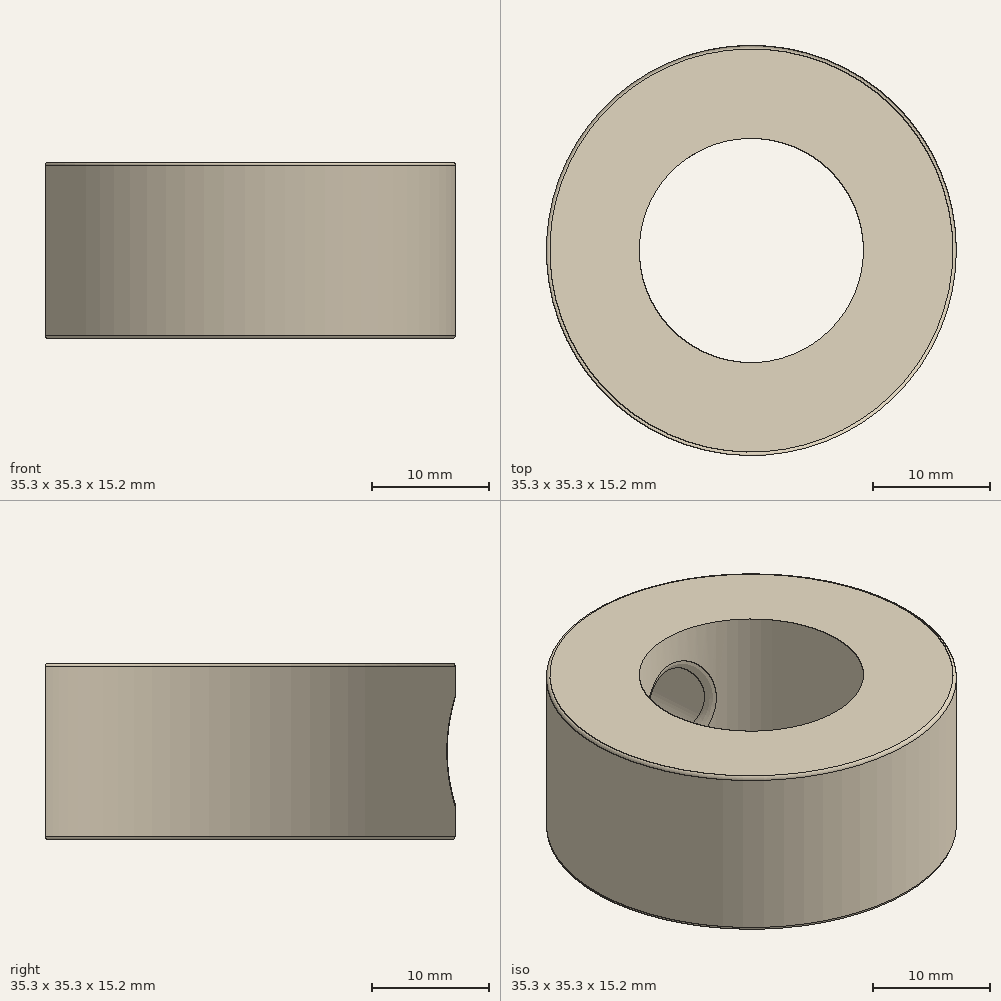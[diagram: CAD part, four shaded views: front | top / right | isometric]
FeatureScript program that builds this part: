
annotation { "Feature Type Name" : "Feature", "Feature Type Description" : "" }
export const myFeature = defineFeature(function(context is Context, id is Id, definition is map)
    precondition{}
    {
        {
            var Q0;
            Q0=qCreatedBy(makeId("Top.planeOp"),FACE);
            var sketch = newSketch(context, id + "F0", { "sketchPlane" : qUnion([Q0])});
            skCircle(sketch, "E0", {"center": v(0, 0) * mm, "radius": 9.65 * mm});
            skCircle(sketch, "E1", {"center": v(0, 0) * mm, "radius": 17.65 * mm});
            skSolve(sketch);
        }
        {
            var Q0;
            Q0 = qSketchRegion(id + "F0", true);
            extrude(context, id + "F1", {"entities" : qUnion([Q0]), "depth" : 15.2 * mm});
        }
        {
            var Q0;
            Q0=makeQuery(id+"F1.opExtrude","CAP_EDGE",EDGE,{"disambiguationData":[OSD([sQuery(id+"F0.wireOp",EDGE,"E1")])],"isStart":false});
            var Q1;
            Q1=makeQuery(id+"F1.opExtrude","SWEPT_FACE",FACE,{"disambiguationData":[OSD([sQuery(id+"F0.wireOp",EDGE,"E1")])]});
            fillet(context, id + "F2", {"entities" : qUnion([Q0, Q1]), "radius" : 0.3 * mm, "tangentPropagation" : true, "allowEdgeOverflow" : false});
        }
        {
            var Q0;
            Q0=qCreatedBy(makeId("Front.planeOp"),FACE);
            var sketch = newSketch(context, id + "F3", { "sketchPlane" : qUnion([Q0])});
            skCircle(sketch, "E2", {"center": v(0, 7.6) * mm, "radius": 3.8 * mm});
            skSolve(sketch);
        }
        {
            var Q0;
            Q0 = qSketchRegion(id + "F3", true);
            extrude(context, id + "F4", {"entities" : qUnion([Q0]), "operationType" : NewBodyOperationType.REMOVE, "oppositeDirection" : true, "depth" : 24 * mm});
        }
        {
            var Q0;
            Q0=makeQuery(id+"F4.boolean.opBoolean","INTERSECT",EDGE,{"derivedFrom":[makeQuery(id+"F1.opExtrude","SWEPT_FACE",FACE,{"disambiguationData":[OSD([sQuery(id+"F0.wireOp",EDGE,"E1")])]}),makeQuery(id+"F4.opExtrude","SWEPT_FACE",FACE,{"disambiguationData":[OSD([sQuery(id+"F3.wireOp",EDGE,"E2")])]})]});
            fillet(context, id + "F5", {"entities" : qUnion([Q0]), "radius" : 1 * mm, "tangentPropagation" : true, "allowEdgeOverflow" : false});
        }
        {
            var Q0;
            Q0=makeQuery(id+"F4.boolean.opBoolean","INTERSECT",EDGE,{"derivedFrom":[makeQuery(id+"F1.opExtrude","SWEPT_FACE",FACE,{"disambiguationData":[OSD([sQuery(id+"F0.wireOp",EDGE,"E0")])]}),makeQuery(id+"F4.opExtrude","SWEPT_FACE",FACE,{"disambiguationData":[OSD([sQuery(id+"F3.wireOp",EDGE,"E2")])]})]});
            fillet(context, id + "F6", {"entities" : qUnion([Q0]), "radius" : 1 * mm, "tangentPropagation" : true, "allowEdgeOverflow" : false});
        }
    });
